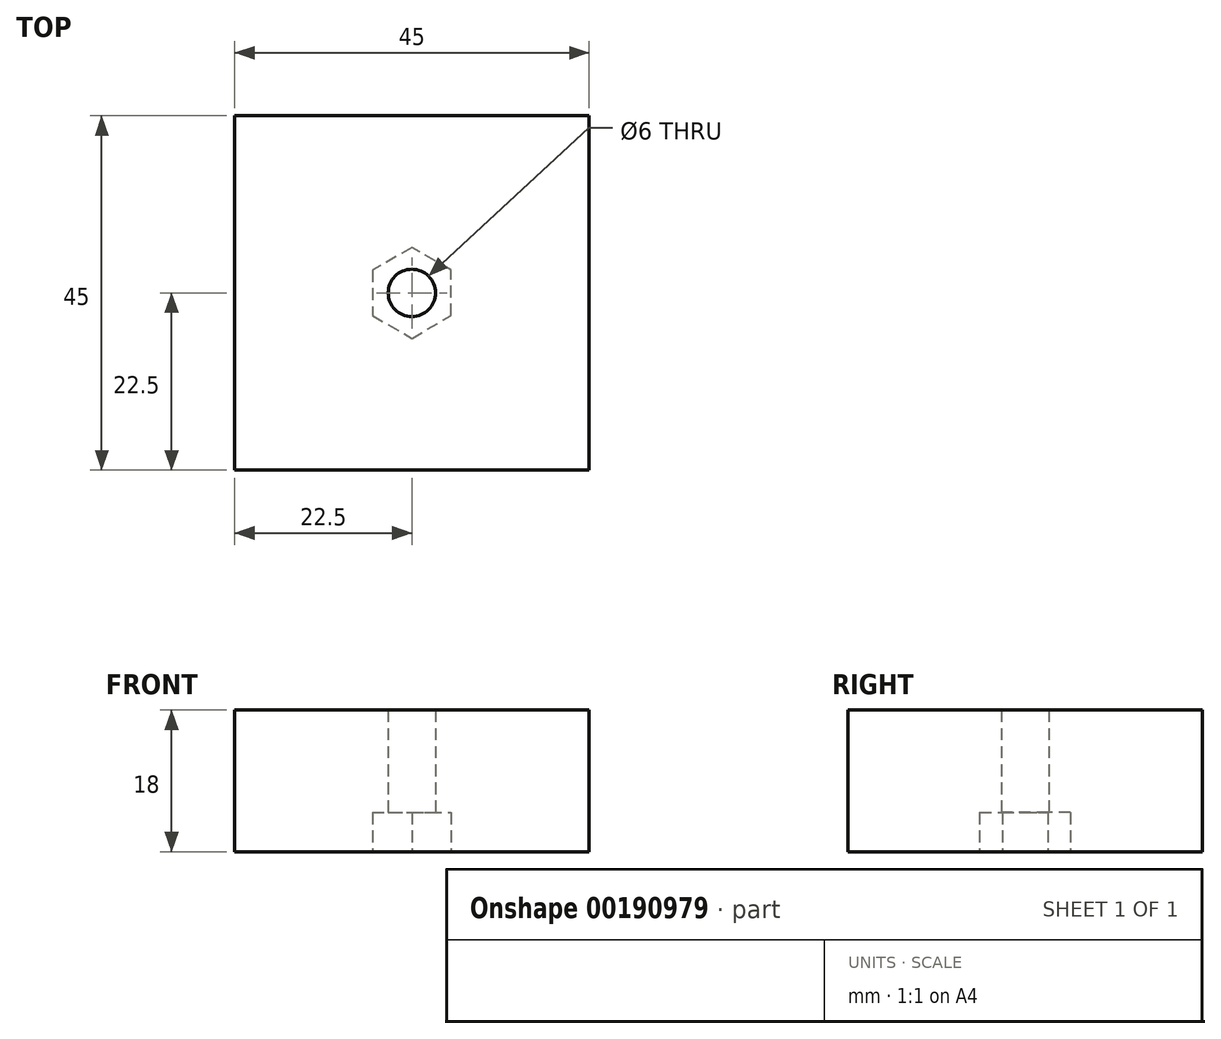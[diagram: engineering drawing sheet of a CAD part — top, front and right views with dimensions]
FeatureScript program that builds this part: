
annotation { "Feature Type Name" : "Feature", "Feature Type Description" : "" }
export const myFeature = defineFeature(function(context is Context, id is Id, definition is map)
    precondition{}
    {
        {
            var Q0;
            Q0=qCreatedBy(makeId("Top.planeOp"),FACE);
            var sketch = newSketch(context, id + "F0", { "sketchPlane" : qUnion([Q0])});
            skLineSegment(sketch, "E0.bottom", {"start": v(-22.5, 22.5) * mm, "end": v(22.5, 22.5) * mm});
            skLineSegment(sketch, "E0.top", {"start": v(-22.5, -22.5) * mm, "end": v(22.5, -22.5) * mm});
            skLineSegment(sketch, "E0.left", {"start": v(-22.5, 22.5) * mm, "end": v(-22.5, -22.5) * mm});
            skLineSegment(sketch, "E0.right", {"start": v(22.5, 22.5) * mm, "end": v(22.5, -22.5) * mm});
            skPoint(sketch, "E0.middle", {"position": v(0, 0) * mm});
            skSolve(sketch);
        }
        {
            var Q0;
            Q0=makeQuery(id+"F0.imprint","IMPRINT",FACE,{"disambiguationData":[TD([[makeQuery(id+"F0.imprint","IMPRINT",EDGE,{"derivedFrom":sQuery(id+"F0.wireOp",EDGE,"E0.bottom")}),-1.0]])]});
            extrude(context, id + "F1", {"entities" : qUnion([Q0]), "depth" : 18 * mm});
        }
        {
            var Q0;
            Q0=qCreatedBy(makeId("Top.planeOp"),FACE);
            var sketch = newSketch(context, id + "F2", { "sketchPlane" : qUnion([Q0])});
            skCircle(sketch, "E1", {"center": v(0, 0) * mm, "radius": 3 * mm});
            skSolve(sketch);
        }
        {
            var Q0;
            Q0=makeQuery(id+"F2.imprint","IMPRINT",FACE,{"disambiguationData":[TD([[makeQuery(id+"F2.imprint","IMPRINT",EDGE,{"derivedFrom":sQuery(id+"F2.wireOp",EDGE,"E1")}),1.0]])]});
            extrude(context, id + "F3", {"entities" : qUnion([Q0]), "operationType" : NewBodyOperationType.REMOVE, "endBound" : BoundingType.THROUGH_ALL, "depth" : 25 * mm});
        }
        {
            var Q0;
            Q0=makeQuery(id+"F1.opExtrude","CAP_FACE",FACE,{"disambiguationData":[OSD([sQuery(id+"F0.wireOp",EDGE,"E0.bottom"),sQuery(id+"F0.wireOp",EDGE,"E0.top"),sQuery(id+"F0.wireOp",EDGE,"E0.left"),sQuery(id+"F0.wireOp",EDGE,"E0.right")])],"isStart":true});
            var sketch = newSketch(context, id + "F4", { "sketchPlane" : qUnion([Q0])});
            skSolve(sketch);
        }
        {
            var Q0;
            Q0=makeQuery(id+"F4.imprint","IMPRINT",FACE,{"disambiguationData":[TD([[makeQuery(id+"F4.imprint","IMPRINT",EDGE,{"derivedFrom":makeQuery(id+"F1.opExtrude","CAP_EDGE",EDGE,{"disambiguationData":[OSD([sQuery(id+"F0.wireOp",EDGE,"E0.bottom")])],"isStart":true})}),1.0]])]});
            var sketch = newSketch(context, id + "F5", { "sketchPlane" : qUnion([Q0])});
            skCircle(sketch, "E2.cCircle", {"center": v(0, 0) * mm, "radius": 5 * mm, "construction": true});
            skLineSegment(sketch, "E2.0", {"start": v(5, 2.89) * mm, "end": v(5, -2.89) * mm});
            skLineSegment(sketch, "E2.1", {"start": v(5, -2.89) * mm, "end": v(0, -5.77) * mm});
            skLineSegment(sketch, "E2.2", {"start": v(0, -5.77) * mm, "end": v(-5, -2.89) * mm});
            skLineSegment(sketch, "E2.3", {"start": v(-5, -2.89) * mm, "end": v(-5, 2.89) * mm});
            skLineSegment(sketch, "E2.4", {"start": v(-5, 2.89) * mm, "end": v(0, 5.77) * mm});
            skLineSegment(sketch, "E2.5", {"start": v(0, 5.77) * mm, "end": v(5, 2.89) * mm});
            skPoint(sketch, "E2.0.midPoint", {"position": v(5, 0) * mm});
            skSolve(sketch);
        }
        {
            var Q0;
            Q0 = qSketchRegion(id + "F5", true);
            extrude(context, id + "F6", {"entities" : qUnion([Q0]), "operationType" : NewBodyOperationType.REMOVE, "oppositeDirection" : true, "depth" : 5 * mm});
        }
    });
